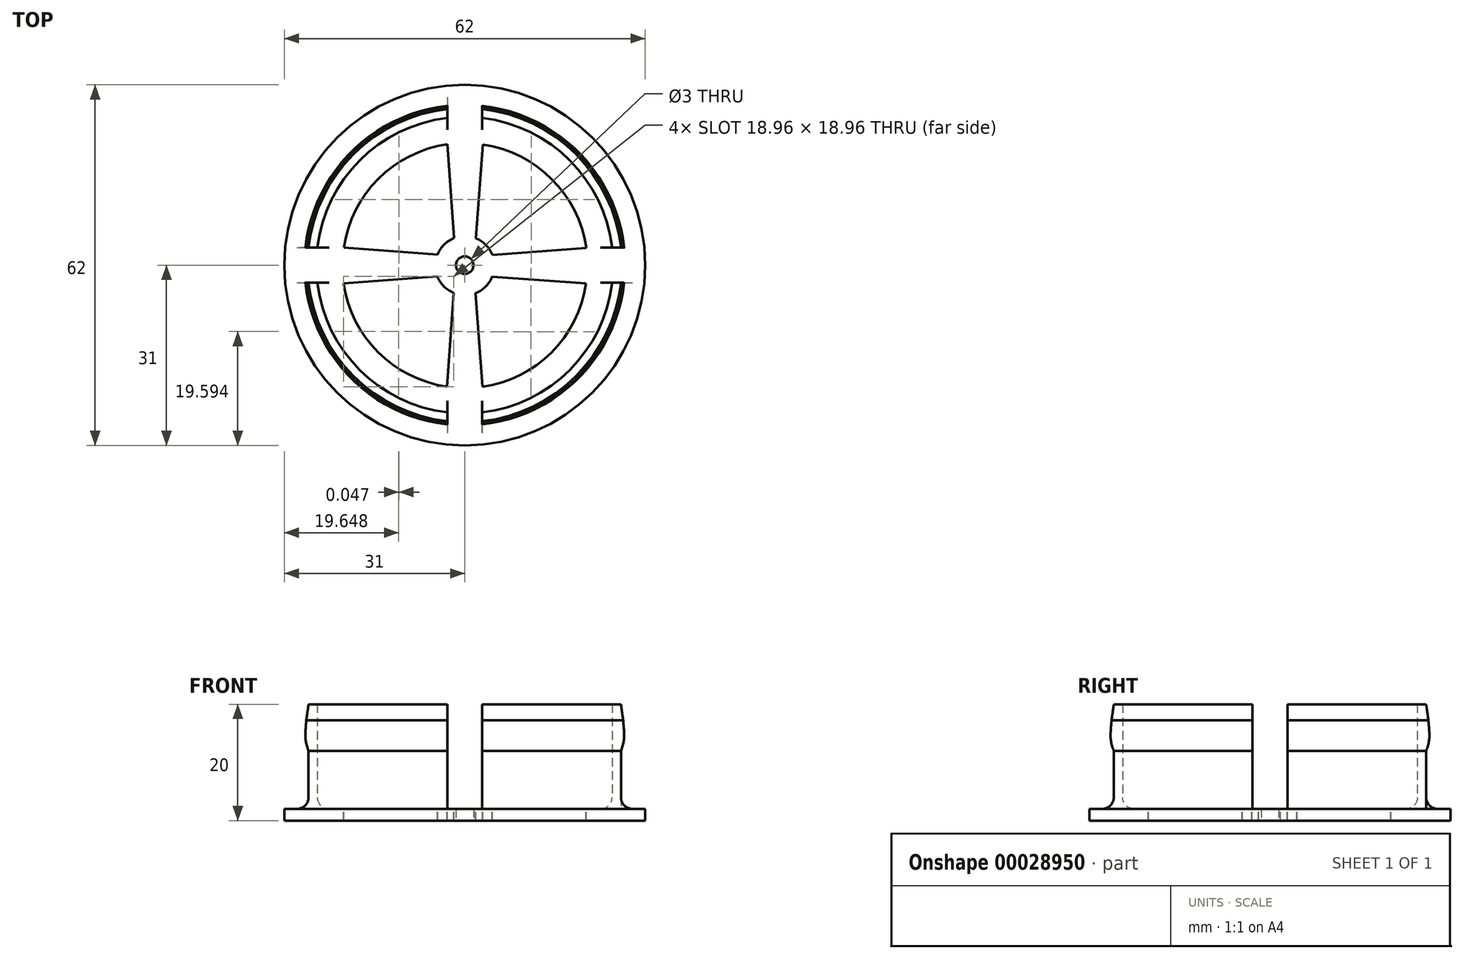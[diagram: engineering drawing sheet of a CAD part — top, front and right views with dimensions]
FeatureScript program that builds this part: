
annotation { "Feature Type Name" : "Feature", "Feature Type Description" : "" }
export const myFeature = defineFeature(function(context is Context, id is Id, definition is map)
    precondition{}
    {
        {
            var Q0;
            Q0=qCreatedBy(makeId("Top.planeOp"),FACE);
            var sketch = newSketch(context, id + "F0", { "sketchPlane" : qUnion([Q0])});
            skCircle(sketch, "E0", {"center": v(0, 0) * mm, "radius": 31 * mm});
            skCircle(sketch, "E1", {"center": v(0, 0) * mm, "radius": 1.5 * mm});
            skCircle(sketch, "E2", {"center": v(0, 0) * mm, "radius": 27 * mm});
            skCircle(sketch, "E3", {"center": v(0, 0) * mm, "radius": 25.5 * mm});
            skSolve(sketch);
        }
        {
            var Q0;
            Q0=makeQuery(id+"F0.imprint","IMPRINT",FACE,{"disambiguationData":[TD([[makeQuery(id+"F0.imprint","IMPRINT",EDGE,{"derivedFrom":sQuery(id+"F0.wireOp",EDGE,"E1")}),-1.0]])]});
            var Q1;
            Q1=makeQuery(id+"F0.imprint","IMPRINT",FACE,{"disambiguationData":[TD([[makeQuery(id+"F0.imprint","IMPRINT",EDGE,{"derivedFrom":sQuery(id+"F0.wireOp",EDGE,"E0")}),1.0]])]});
            extrude(context, id + "F1", {"entities" : qUnion([Q0, Q1]), "depth" : 2 * mm});
        }
        {
            var Q0;
            Q0=makeQuery(id+"F0.imprint","IMPRINT",FACE,{"disambiguationData":[TD([[makeQuery(id+"F0.imprint","IMPRINT",EDGE,{"derivedFrom":sQuery(id+"F0.wireOp",EDGE,"E2")}),1.0]])]});
            extrude(context, id + "F2", {"entities" : qUnion([Q0]), "depth" : 20 * mm});
        }
        {
            var Q0;
            Q0=makeQuery(id+"F2.opExtrude","CAP_FACE",FACE,{"disambiguationData":[OSD([sQuery(id+"F0.wireOp",EDGE,"E2"),sQuery(id+"F0.wireOp",EDGE,"E3")])],"isStart":false});
            var sketch = newSketch(context, id + "F3", { "sketchPlane" : qUnion([Q0])});
            skPoint(sketch, "E4", {"position": v(-27, 0) * mm});
            skSolve(sketch);
        }
        {
            var Q0;
            Q0=qCreatedBy(makeId("Front.planeOp"),FACE);
            var sketch = newSketch(context, id + "F4", { "sketchPlane" : qUnion([Q0])});
            skLineSegment(sketch, "E5", {"start": v(-27.39, 17.27) * mm, "end": v(-27, 20) * mm});
            skLineSegment(sketch, "E6", {"start": v(-27, 20) * mm, "end": v(-27, 12) * mm});
            skFitSpline(sketch, "E7", {"points": [v(-27.39, 17.27) * mm, v(-27.5, 13.79) * mm, v(-27, 12) * mm], "startDerivative": vector(-0.82, -10.12) * mm, "endDerivative": vector(1.94, -5.37) * mm});
            skSolve(sketch);
        }
        {
            var Q0;
            Q0=makeQuery(id+"F4.imprint","IMPRINT",FACE,{"disambiguationData":[TD([[makeQuery(id+"F4.imprint","IMPRINT",EDGE,{"derivedFrom":sQuery(id+"F4.wireOp",EDGE,"E5")}),-1.0]])]});
            var Q1;
            Q1=makeQuery(id+"F2.opExtrude","CAP_EDGE",EDGE,{"disambiguationData":[OSD([sQuery(id+"F0.wireOp",EDGE,"E3")])],"isStart":false});
            revolve(context, id + "F5", {"operationType" : NewBodyOperationType.ADD, "entities" : qUnion([Q0]), "axis" : qUnion([Q1]), "revolveType" : RevolveType.FULL});
        }
        {
            var Q0;
            Q0=qCreatedBy(makeId("Right.planeOp"),FACE);
            cPlane(context, id + "F6", {"entities" : qUnion([Q0]), "cplaneType" : CPlaneType.OFFSET, "offset" : 30 * mm, "width" : 150 * mm, "height" : 150 * mm});
        }
        {
            var Q0;
            Q0=qCreatedBy(id+"F6.planeOp",FACE);
            var sketch = newSketch(context, id + "F7", { "sketchPlane" : qUnion([Q0])});
            skLineSegment(sketch, "E8.bottom", {"start": v(-3, 2) * mm, "end": v(3, 2) * mm});
            skLineSegment(sketch, "E8.top", {"start": v(-3, 20) * mm, "end": v(3, 20) * mm});
            skLineSegment(sketch, "E8.left", {"start": v(-3, 2) * mm, "end": v(-3, 20) * mm});
            skLineSegment(sketch, "E8.right", {"start": v(3, 2) * mm, "end": v(3, 20) * mm});
            skLineSegment(sketch, "E9.0", {"start": v(-31, 2) * mm, "end": v(31, 2) * mm, "construction": true});
            skLineSegment(sketch, "E10.1", {"start": v(27, 20) * mm, "end": v(-27, 20) * mm, "construction": true});
            skSolve(sketch);
        }
        {
            var Q0;
            Q0=qCreatedBy(makeId("Front.planeOp"),FACE);
            var sketch = newSketch(context, id + "F8", { "sketchPlane" : qUnion([Q0])});
            skLineSegment(sketch, "E11", {"start": v(25.5, 2) * mm, "end": v(23.5, 2) * mm});
            skLineSegment(sketch, "E12", {"start": v(25.5, 4) * mm, "end": v(25.5, 2) * mm});
            skArc(sketch, "E13", {"start": v(23.5, 2) * mm, "mid": v(24.91, 2.59) * mm, "end": v(25.5, 4) * mm});
            skSolve(sketch);
        }
        {
            var Q0;
            Q0 = qSketchRegion(id + "F8", true);
            var Q1;
            Q1=sQuery(id+"F0.wireOp",EDGE,"E2");
            revolve(context, id + "F9", {"entities" : qUnion([Q0]), "axis" : qUnion([Q1]), "revolveType" : RevolveType.FULL});
        }
        {
            var Q0;
            Q0 = qSketchRegion(id + "F7", true);
            extrude(context, id + "F10", {"entities" : qUnion([Q0]), "operationType" : NewBodyOperationType.REMOVE, "endBound" : BoundingType.THROUGH_ALL, "oppositeDirection" : true, "depth" : 25 * mm});
        }
        {
            var Q0;
            Q0=qCreatedBy(makeId("Front.planeOp"),FACE);
            cPlane(context, id + "F11", {"entities" : qUnion([Q0]), "cplaneType" : CPlaneType.OFFSET, "offset" : 30 * mm, "width" : 150 * mm, "height" : 150 * mm});
        }
        {
            var Q0;
            Q0=qCreatedBy(id+"F11.planeOp",FACE);
            var sketch = newSketch(context, id + "F12", { "sketchPlane" : qUnion([Q0])});
            skLineSegment(sketch, "E14.0", {"start": v(26.83, 20) * mm, "end": v(-26.83, 20) * mm, "construction": true});
            skLineSegment(sketch, "E14.1", {"start": v(-31, 2) * mm, "end": v(31, 2) * mm, "construction": true});
            skLineSegment(sketch, "E15.bottom", {"start": v(3, 2) * mm, "end": v(-3, 2) * mm});
            skLineSegment(sketch, "E15.top", {"start": v(3, 20) * mm, "end": v(-3, 20) * mm});
            skLineSegment(sketch, "E15.left", {"start": v(3, 2) * mm, "end": v(3, 20) * mm});
            skLineSegment(sketch, "E15.right", {"start": v(-3, 2) * mm, "end": v(-3, 20) * mm});
            skSolve(sketch);
        }
        {
            var Q0;
            Q0 = qSketchRegion(id + "F12", true);
            extrude(context, id + "F13", {"entities" : qUnion([Q0]), "operationType" : NewBodyOperationType.REMOVE, "endBound" : BoundingType.THROUGH_ALL, "oppositeDirection" : true, "depth" : 25 * mm});
        }
        {
            var Q0;
            Q0=makeQuery(id+"F1.opExtrude","SWEPT_BODY",BODY,{"disambiguationData":[OSD([sQuery(id+"F0.wireOp",EDGE,"E0"),sQuery(id+"F0.wireOp",EDGE,"E2")])]});
            var Q1;
            Q1=makeQuery(id+"F1.opExtrude","SWEPT_BODY",BODY,{"disambiguationData":[OSD([sQuery(id+"F0.wireOp",EDGE,"E1"),sQuery(id+"F0.wireOp",EDGE,"E3")])]});
            var Q2;
            Q2=makeQuery(id+"F2.opExtrude","SWEPT_BODY",BODY,{"disambiguationData":[OSD([sQuery(id+"F0.wireOp",EDGE,"E2"),sQuery(id+"F0.wireOp",EDGE,"E3")])]});
            var Q3;
            Q3=makeQuery(id+"F13.boolean.opBoolean","SPLIT",BODY,{"disambiguationData":[OD(0.0)],"derivedFrom":makeQuery(id+"F10.boolean.opBoolean","SPLIT",BODY,{"disambiguationData":[OD(0.0)],"derivedFrom":makeQuery(id+"F9.opRevolve","SWEPT_BODY",BODY,{"disambiguationData":[OSD([sQuery(id+"F8.wireOp",EDGE,"E11"),sQuery(id+"F8.wireOp",EDGE,"a499a142-f307-41e8-b9c9-25aaca2defeb"),sQuery(id+"F8.wireOp",EDGE,"E12")])]})})});
            var Q4;
            Q4=makeQuery(id+"F13.boolean.opBoolean","SPLIT",BODY,{"disambiguationData":[OD(1.0)],"derivedFrom":makeQuery(id+"F10.boolean.opBoolean","SPLIT",BODY,{"disambiguationData":[OD(0.0)],"derivedFrom":makeQuery(id+"F9.opRevolve","SWEPT_BODY",BODY,{"disambiguationData":[OSD([sQuery(id+"F8.wireOp",EDGE,"E11"),sQuery(id+"F8.wireOp",EDGE,"a499a142-f307-41e8-b9c9-25aaca2defeb"),sQuery(id+"F8.wireOp",EDGE,"E12")])]})})});
            var Q5;
            Q5=makeQuery(id+"F13.boolean.opBoolean","SPLIT",BODY,{"disambiguationData":[OD(0.0)],"derivedFrom":makeQuery(id+"F10.boolean.opBoolean","SPLIT",BODY,{"disambiguationData":[OD(1.0)],"derivedFrom":makeQuery(id+"F9.opRevolve","SWEPT_BODY",BODY,{"disambiguationData":[OSD([sQuery(id+"F8.wireOp",EDGE,"E11"),sQuery(id+"F8.wireOp",EDGE,"a499a142-f307-41e8-b9c9-25aaca2defeb"),sQuery(id+"F8.wireOp",EDGE,"E12")])]})})});
            var Q6;
            Q6=makeQuery(id+"F13.boolean.opBoolean","SPLIT",BODY,{"disambiguationData":[OD(1.0)],"derivedFrom":makeQuery(id+"F10.boolean.opBoolean","SPLIT",BODY,{"disambiguationData":[OD(1.0)],"derivedFrom":makeQuery(id+"F9.opRevolve","SWEPT_BODY",BODY,{"disambiguationData":[OSD([sQuery(id+"F8.wireOp",EDGE,"E11"),sQuery(id+"F8.wireOp",EDGE,"a499a142-f307-41e8-b9c9-25aaca2defeb"),sQuery(id+"F8.wireOp",EDGE,"E12")])]})})});
            booleanBodies(context, id + "F14", {"operationType" : BooleanOperationType.UNION, "tools" : qUnion([Q0, Q1, Q2, Q3, Q4, Q5, Q6])});
        }
        {
            var Q0;
            {var subQ0=sQuery(id+"F0.wireOp",EDGE,"E2");var subQ3=makeQuery(id+"F10.opExtrude","SWEPT_FACE",FACE,{"disambiguationData":[OSD([sQuery(id+"F7.wireOp",EDGE,"E8.left")])]});Q0=makeQuery(id+"F14.opBoolean","SPLIT",EDGE,{"disambiguationData":[TD([makeQuery(id+"F10.boolean.opBoolean","COPY",FACE,{"disambiguationData":[OD(1.0)],"derivedFrom":subQ3})])],"derivedFrom":makeQuery(id+"F1.opExtrude","CAP_EDGE",EDGE,{"disambiguationData":[OSD([subQ0])],"isStart":false})});}
            var Q1;
            {var subQ0=sQuery(id+"F0.wireOp",EDGE,"E2");var subQ3=makeQuery(id+"F10.opExtrude","SWEPT_FACE",FACE,{"disambiguationData":[OSD([sQuery(id+"F7.wireOp",EDGE,"E8.left")])]});Q1=makeQuery(id+"F14.opBoolean","SPLIT",EDGE,{"disambiguationData":[TD([makeQuery(id+"F10.boolean.opBoolean","COPY",FACE,{"disambiguationData":[OD(0.0)],"derivedFrom":subQ3})])],"derivedFrom":makeQuery(id+"F1.opExtrude","CAP_EDGE",EDGE,{"disambiguationData":[OSD([subQ0])],"isStart":false})});}
            var Q2;
            {var subQ0=sQuery(id+"F0.wireOp",EDGE,"E2");var subQ3=makeQuery(id+"F10.opExtrude","SWEPT_FACE",FACE,{"disambiguationData":[OSD([sQuery(id+"F7.wireOp",EDGE,"E8.right")])]});Q2=makeQuery(id+"F14.opBoolean","SPLIT",EDGE,{"disambiguationData":[TD([makeQuery(id+"F10.boolean.opBoolean","COPY",FACE,{"disambiguationData":[OD(1.0)],"derivedFrom":subQ3})])],"derivedFrom":makeQuery(id+"F1.opExtrude","CAP_EDGE",EDGE,{"disambiguationData":[OSD([subQ0])],"isStart":false})});}
            var Q3;
            {var subQ0=sQuery(id+"F0.wireOp",EDGE,"E2");var subQ3=makeQuery(id+"F10.opExtrude","SWEPT_FACE",FACE,{"disambiguationData":[OSD([sQuery(id+"F7.wireOp",EDGE,"E8.right")])]});Q3=makeQuery(id+"F14.opBoolean","SPLIT",EDGE,{"disambiguationData":[TD([makeQuery(id+"F10.boolean.opBoolean","COPY",FACE,{"disambiguationData":[OD(0.0)],"derivedFrom":subQ3})])],"derivedFrom":makeQuery(id+"F1.opExtrude","CAP_EDGE",EDGE,{"disambiguationData":[OSD([subQ0])],"isStart":false})});}
            fillet(context, id + "F15", {"entities" : qUnion([Q0, Q1, Q2, Q3]), "radius" : 2 * mm, "tangentPropagation" : true, "allowEdgeOverflow" : false});
        }
        {
            var Q0;
            {var subQ0=makeQuery(id+"F10.opExtrude","SWEPT_FACE",FACE,{"disambiguationData":[OSD([sQuery(id+"F7.wireOp",EDGE,"E8.bottom")])]});var subQ1=makeQuery(id+"F13.opExtrude","SWEPT_FACE",FACE,{"disambiguationData":[OSD([sQuery(id+"F12.wireOp",EDGE,"E15.bottom")])]});Q0=makeQuery(id+"F14.opBoolean","MERGE",FACE,{"derivedFrom":[makeQuery(id+"F10.boolean.opBoolean","COPY",FACE,{"disambiguationData":[OD(0.0)],"derivedFrom":subQ0}),makeQuery(id+"F10.boolean.opBoolean","COPY",FACE,{"disambiguationData":[OD(1.0)],"derivedFrom":subQ0}),makeQuery(id+"F1.opExtrude","CAP_FACE",FACE,{"disambiguationData":[OSD([sQuery(id+"F0.wireOp",EDGE,"E0"),sQuery(id+"F0.wireOp",EDGE,"E2")])],"isStart":false}),makeQuery(id+"F1.opExtrude","CAP_FACE",FACE,{"disambiguationData":[OSD([sQuery(id+"F0.wireOp",EDGE,"E1"),sQuery(id+"F0.wireOp",EDGE,"E3")])],"isStart":false}),makeQuery(id+"F13.boolean.opBoolean","COPY",FACE,{"disambiguationData":[OD(0.0)],"derivedFrom":subQ1}),makeQuery(id+"F13.boolean.opBoolean","COPY",FACE,{"disambiguationData":[OD(1.0)],"derivedFrom":subQ1})]});}
            var sketch = newSketch(context, id + "F16", { "sketchPlane" : qUnion([Q0])});
            skCircle(sketch, "E16", {"center": v(0, 0) * mm, "radius": 5 * mm, "construction": true});
            skCircle(sketch, "E17", {"center": v(0, 0) * mm, "radius": 21 * mm, "construction": true});
            skLineSegment(sketch, "E18", {"start": v(-4.65, 1.83) * mm, "end": v(-20.78, 3) * mm});
            skLineSegment(sketch, "E19", {"start": v(-1.83, 4.65) * mm, "end": v(-3, 20.78) * mm});
            skArc(sketch, "E20", {"start": v(-3, 20.78) * mm, "mid": v(-14.85, 14.85) * mm, "end": v(-20.78, 3) * mm});
            skArc(sketch, "E21", {"start": v(-1.83, 4.65) * mm, "mid": v(-3.54, 3.54) * mm, "end": v(-4.65, 1.83) * mm});
            skLineSegment(sketch, "E22.1.0", {"start": v(-4.7, -1.93) * mm, "end": v(-20.83, -3.1) * mm});
            skArc(sketch, "E22.1.1", {"start": v(-20.83, -3.1) * mm, "mid": v(-14.9, -14.95) * mm, "end": v(-3.05, -20.88) * mm});
            skLineSegment(sketch, "E22.1.2", {"start": v(-1.87, -4.75) * mm, "end": v(-3.05, -20.88) * mm});
            skArc(sketch, "E22.1.3", {"start": v(-4.7, -1.93) * mm, "mid": v(-3.58, -3.64) * mm, "end": v(-1.87, -4.75) * mm});
            skLineSegment(sketch, "E22.2.0", {"start": v(1.88, -4.8) * mm, "end": v(3.05, -20.93) * mm});
            skArc(sketch, "E22.2.1", {"start": v(3.05, -20.93) * mm, "mid": v(14.9, -15) * mm, "end": v(20.84, -3.15) * mm});
            skLineSegment(sketch, "E22.2.2", {"start": v(4.7, -1.97) * mm, "end": v(20.84, -3.15) * mm});
            skArc(sketch, "E22.2.3", {"start": v(1.88, -4.8) * mm, "mid": v(3.59, -3.68) * mm, "end": v(4.7, -1.97) * mm});
            skLineSegment(sketch, "E22.3.0", {"start": v(4.75, 1.78) * mm, "end": v(20.88, 2.95) * mm});
            skArc(sketch, "E22.3.1", {"start": v(20.88, 2.95) * mm, "mid": v(14.95, 14.8) * mm, "end": v(3.1, 20.74) * mm});
            skLineSegment(sketch, "E22.3.2", {"start": v(1.93, 4.6) * mm, "end": v(3.1, 20.74) * mm});
            skArc(sketch, "E22.3.3", {"start": v(4.75, 1.78) * mm, "mid": v(3.64, 3.49) * mm, "end": v(1.93, 4.6) * mm});
            skPoint(sketch, "E22.center", {"position": v(0.03, -0.07) * mm});
            skSolve(sketch);
        }
        {
            var Q0;
            Q0 = qSketchRegion(id + "F16", true);
            extrude(context, id + "F17", {"entities" : qUnion([Q0]), "operationType" : NewBodyOperationType.REMOVE, "oppositeDirection" : true, "depth" : 25 * mm});
        }
    });
